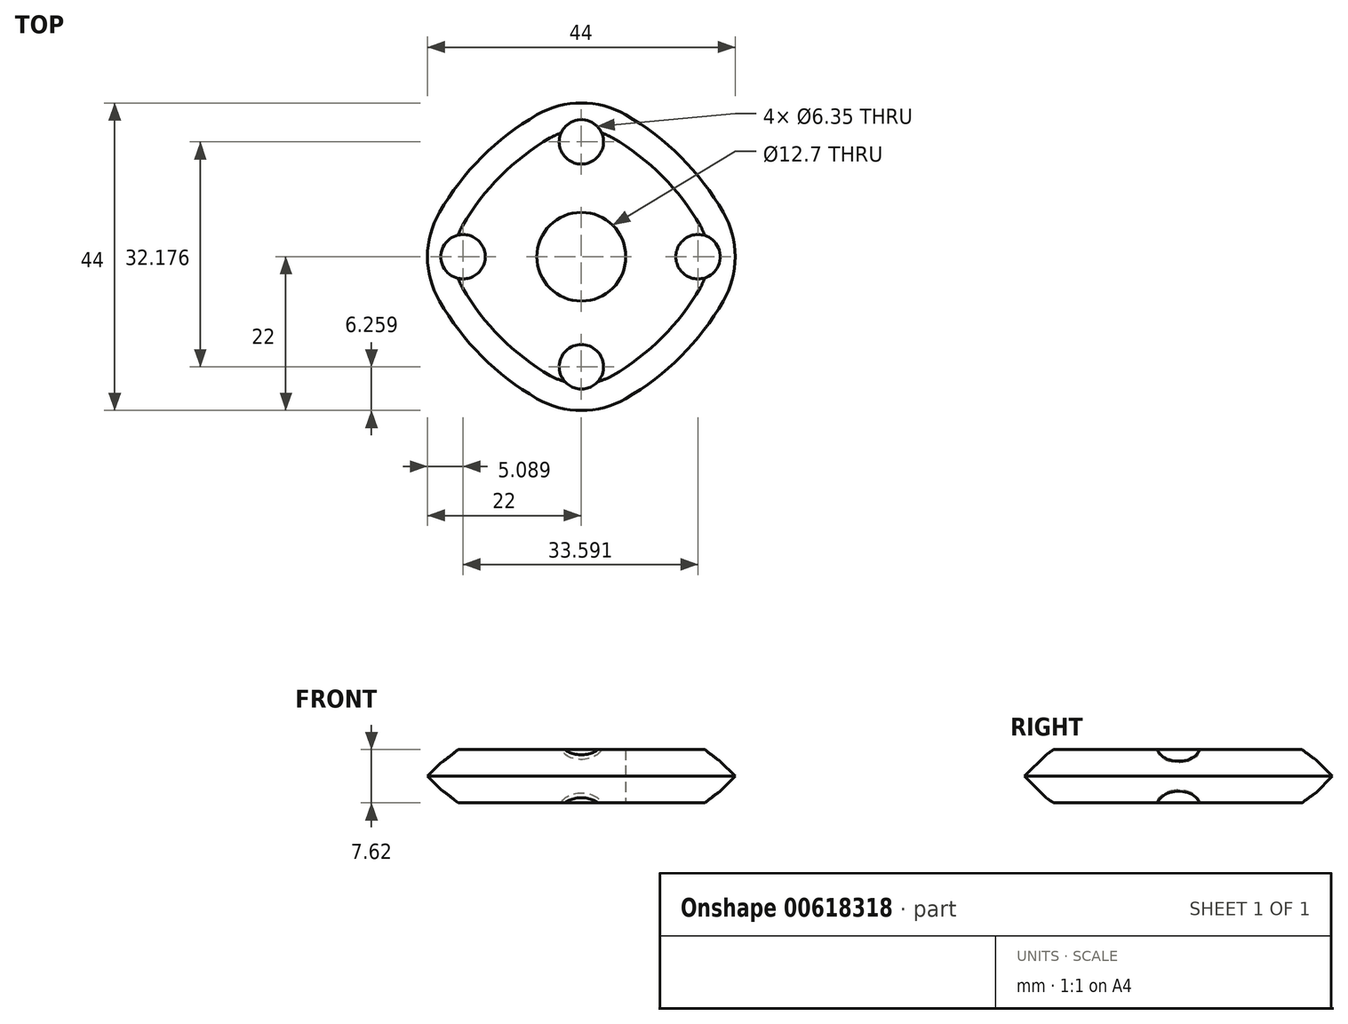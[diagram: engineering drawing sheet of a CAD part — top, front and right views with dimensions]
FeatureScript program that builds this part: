
annotation { "Feature Type Name" : "Feature", "Feature Type Description" : "" }
export const myFeature = defineFeature(function(context is Context, id is Id, definition is map)
    precondition{}
    {
        {
            var Q0;
            Q0=qCreatedBy(makeId("Top.planeOp"),FACE);
            var sketch = newSketch(context, id + "F0", { "sketchPlane" : qUnion([Q0])});
            skLineSegment(sketch, "E0.bottom", {"start": v(25.4, 25.4) * mm, "end": v(-25.4, 25.4) * mm});
            skLineSegment(sketch, "E0.top", {"start": v(25.4, -25.4) * mm, "end": v(-25.4, -25.4) * mm});
            skLineSegment(sketch, "E0.left", {"start": v(25.4, 25.4) * mm, "end": v(25.4, -25.4) * mm});
            skLineSegment(sketch, "E0.right", {"start": v(-25.4, 25.4) * mm, "end": v(-25.4, -25.4) * mm});
            skPoint(sketch, "E0.middle", {"position": v(0, 0) * mm});
            skCircle(sketch, "E1", {"center": v(0, 0) * mm, "radius": 6.35 * mm});
            skSolve(sketch);
        }
        {
            var Q0;
            Q0=makeQuery(id+"F0.imprint","IMPRINT",FACE,{"disambiguationData":[TD([[makeQuery(id+"F0.imprint","IMPRINT",EDGE,{"derivedFrom":sQuery(id+"F0.wireOp",EDGE,"E0.bottom")}),1.0]])]});
            extrude(context, id + "F1", {"entities" : qUnion([Q0]), "depth" : 7.62 * mm, "offsetDistance" : 25.4 * mm});
        }
        {
            var Q0;
            Q0=makeQuery(id+"F1.opExtrude","SWEPT_EDGE",EDGE,{"disambiguationData":[OSD([sQuery(id+"F0.wireOp",EDGE,"E0.top"),sQuery(id+"F0.wireOp",EDGE,"E0.left")])]});
            var Q1;
            Q1=makeQuery(id+"F1.opExtrude","SWEPT_EDGE",EDGE,{"disambiguationData":[OSD([sQuery(id+"F0.wireOp",EDGE,"E0.top"),sQuery(id+"F0.wireOp",EDGE,"E0.right")])]});
            var Q2;
            Q2=makeQuery(id+"F1.opExtrude","SWEPT_EDGE",EDGE,{"disambiguationData":[OSD([sQuery(id+"F0.wireOp",EDGE,"E0.bottom"),sQuery(id+"F0.wireOp",EDGE,"E0.right")])]});
            var Q3;
            Q3=makeQuery(id+"F1.opExtrude","SWEPT_EDGE",EDGE,{"disambiguationData":[OSD([sQuery(id+"F0.wireOp",EDGE,"E0.bottom"),sQuery(id+"F0.wireOp",EDGE,"E0.left")])]});
            fillet(context, id + "F2", {"entities" : qUnion([Q0, Q1, Q2, Q3]), "radius" : 38.1 * mm, "tangentPropagation" : true, "allowEdgeOverflow" : false});
        }
        {
            var Q0;
            Q0=qCreatedBy(makeId("Top.planeOp"),FACE);
            var sketch = newSketch(context, id + "F3", { "sketchPlane" : qUnion([Q0])});
            skPoint(sketch, "E2", {"position": v(0, 16.44) * mm});
            skPoint(sketch, "E3", {"position": v(16.68, 0) * mm});
            skPoint(sketch, "E4", {"position": v(0, -15.74) * mm});
            skPoint(sketch, "E5", {"position": v(-16.91, 0) * mm});
            skSolve(sketch);
        }
        {
            var Q0;
            Q0=sQuery(id+"F3.wireOp",VERTEX,"E2");
            var Q1;
            Q1=sQuery(id+"F3.wireOp",VERTEX,"E5");
            var Q2;
            Q2=sQuery(id+"F3.wireOp",VERTEX,"E4");
            var Q3;
            Q3=sQuery(id+"F3.wireOp",VERTEX,"E3");
            var Q4;
            Q4=makeQuery(id+"F1.opExtrude","SWEPT_BODY",BODY,{"disambiguationData":[OSD([sQuery(id+"F0.wireOp",EDGE,"E0.bottom"),sQuery(id+"F0.wireOp",EDGE,"E0.top"),sQuery(id+"F0.wireOp",EDGE,"E0.left"),sQuery(id+"F0.wireOp",EDGE,"E0.right"),sQuery(id+"F0.wireOp",EDGE,"E1")])]});
            hole(context, id + "F4", {"style" : HoleStyle.SIMPLE, "endStyle" : HoleEndStyle.THROUGH, "oppositeDirection" : true, "holeDiameter" : 6.35 * mm, "majorDiameter" : 6.35 * mm, "isTappedThrough" : true, "tappedDepth" : 12.7 * mm, "tapClearance" : 3, "locations" : qUnion([Q0, Q1, Q2, Q3]), "scope" : qUnion([Q4])});
        }
        {
            var Q0;
            {var subQ0=sQuery(id+"F0.wireOp",EDGE,"E0.top");Q0=makeQuery(id+"F2.opFillet","BLEND_EDGE",EDGE,{"blendedFrom":[makeQuery(id+"F1.opExtrude","SWEPT_EDGE",EDGE,{"disambiguationData":[OSD([subQ0,sQuery(id+"F0.wireOp",EDGE,"E0.left")])]}),makeQuery(id+"F1.opExtrude","SWEPT_EDGE",EDGE,{"disambiguationData":[OSD([subQ0,sQuery(id+"F0.wireOp",EDGE,"E0.right")])]})],"blendedInto":[]});}
            var Q1;
            {var subQ0=sQuery(id+"F0.wireOp",EDGE,"E0.left");Q1=makeQuery(id+"F2.opFillet","BLEND_EDGE",EDGE,{"blendedFrom":[makeQuery(id+"F1.opExtrude","SWEPT_EDGE",EDGE,{"disambiguationData":[OSD([sQuery(id+"F0.wireOp",EDGE,"E0.bottom"),subQ0])]}),makeQuery(id+"F1.opExtrude","SWEPT_EDGE",EDGE,{"disambiguationData":[OSD([sQuery(id+"F0.wireOp",EDGE,"E0.top"),subQ0])]})],"blendedInto":[]});}
            var Q2;
            {var subQ0=sQuery(id+"F0.wireOp",EDGE,"E0.right");Q2=makeQuery(id+"F2.opFillet","BLEND_EDGE",EDGE,{"blendedFrom":[makeQuery(id+"F1.opExtrude","SWEPT_EDGE",EDGE,{"disambiguationData":[OSD([sQuery(id+"F0.wireOp",EDGE,"E0.bottom"),subQ0])]}),makeQuery(id+"F1.opExtrude","SWEPT_EDGE",EDGE,{"disambiguationData":[OSD([sQuery(id+"F0.wireOp",EDGE,"E0.top"),subQ0])]})],"blendedInto":[]});}
            var Q3;
            {var subQ0=sQuery(id+"F0.wireOp",EDGE,"E0.bottom");Q3=makeQuery(id+"F2.opFillet","BLEND_EDGE",EDGE,{"blendedFrom":[makeQuery(id+"F1.opExtrude","SWEPT_EDGE",EDGE,{"disambiguationData":[OSD([subQ0,sQuery(id+"F0.wireOp",EDGE,"E0.left")])]}),makeQuery(id+"F1.opExtrude","SWEPT_EDGE",EDGE,{"disambiguationData":[OSD([subQ0,sQuery(id+"F0.wireOp",EDGE,"E0.right")])]})],"blendedInto":[]});}
            fillet(context, id + "F5", {"entities" : qUnion([Q0, Q1, Q2, Q3]), "radius" : 12.7 * mm, "tangentPropagation" : true, "allowEdgeOverflow" : false});
        }
        {
            var Q0;
            {var subQ0=sQuery(id+"F0.wireOp",EDGE,"E0.left");var subQ1=sQuery(id+"F0.wireOp",EDGE,"E0.top");Q0=makeQuery(id+"F2.opFillet","BLEND_EDGE",EDGE,{"blendedFrom":[makeQuery(id+"F1.opExtrude","SWEPT_EDGE",EDGE,{"disambiguationData":[OSD([subQ1,subQ0])]}),makeQuery(id+"F1.opExtrude","CAP_FACE",FACE,{"disambiguationData":[OSD([sQuery(id+"F0.wireOp",EDGE,"E0.bottom"),subQ1,subQ0,sQuery(id+"F0.wireOp",EDGE,"E0.right"),sQuery(id+"F0.wireOp",EDGE,"E1")])],"isStart":false})],"blendedInto":[makeQuery(id+"F1.opExtrude","CAP_FACE",FACE,{"disambiguationData":[OSD([sQuery(id+"F0.wireOp",EDGE,"E0.bottom"),subQ1,subQ0,sQuery(id+"F0.wireOp",EDGE,"E0.right"),sQuery(id+"F0.wireOp",EDGE,"E1")])],"isStart":false})]});}
            var Q1;
            {var subQ0=sQuery(id+"F0.wireOp",EDGE,"E0.left");var subQ1=sQuery(id+"F0.wireOp",EDGE,"E0.top");Q1=makeQuery(id+"F2.opFillet","BLEND_EDGE",EDGE,{"blendedFrom":[makeQuery(id+"F1.opExtrude","SWEPT_EDGE",EDGE,{"disambiguationData":[OSD([subQ1,subQ0])]}),makeQuery(id+"F1.opExtrude","CAP_FACE",FACE,{"disambiguationData":[OSD([sQuery(id+"F0.wireOp",EDGE,"E0.bottom"),subQ1,subQ0,sQuery(id+"F0.wireOp",EDGE,"E0.right"),sQuery(id+"F0.wireOp",EDGE,"E1")])],"isStart":true})],"blendedInto":[makeQuery(id+"F1.opExtrude","CAP_FACE",FACE,{"disambiguationData":[OSD([sQuery(id+"F0.wireOp",EDGE,"E0.bottom"),subQ1,subQ0,sQuery(id+"F0.wireOp",EDGE,"E0.right"),sQuery(id+"F0.wireOp",EDGE,"E1")])],"isStart":true})]});}
            chamfer(context, id + "F6", {"entities" : qUnion([Q0, Q1]), "width" : 3.8 * mm, "tangentPropagation" : true});
        }
    });
